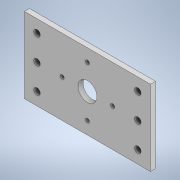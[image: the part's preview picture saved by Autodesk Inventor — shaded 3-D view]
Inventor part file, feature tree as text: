
AUTODESK INVENTOR PART (.ipt)
format: ipt  version: 2020 (Build 240168000, 168)  size: 137,728 bytes
history: native  units: in
note: dims shown in document units (in); Inventor stores cm internally (conversion verified against a paired STEP export)
features: extrude x1, sketch x1
ambient origin geometry x8: Origin, YZ Plane, XZ Plane, XY Plane, X Axis, Y Axis, Z Axis, Center Point
bodies: Body1 (feature_tree)
feature tree (2):
  extrude  "Extrusion2"  Depth=3.0in
  sketch  "Sketch1"  dims[d0=5.0in d1=3.0in d2=0.75in d3=1.5in d4=2.5in d5=0.159in d6=1.0in d7=2.5in d8=0.159in d9=1.0in d10=1.5in d11=0.7874in d13=2.0in d14=0.3937in d16=1.0in d18=0.7874in d20=2.0in d21=0.3937in d23=1.0in d25=0.256in d26=0.5in d27=0.5in d28=1.1811in d30=1.0in d31=0.3937in d33=1.0in d37=0.7874in d39=4.0in d40=0.3937in d42=1.0in d44=0.2in d45=0.0in]
